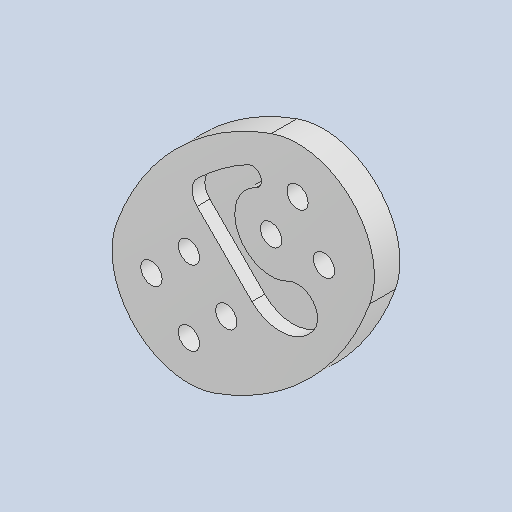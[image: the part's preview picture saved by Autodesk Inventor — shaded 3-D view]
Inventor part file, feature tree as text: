
AUTODESK INVENTOR PART (.ipt)
format: ipt  version: 2023.1 (Build 271208000, 208)  size: 332,800 bytes
history: native  units: mm
features: extrude x2, sketch x2, other x1, projected_geometry x1
ambient origin geometry x8: Origin, YZ Plane, XZ Plane, XY Plane, X Axis, Y Axis, Z Axis, Center Point
bodies: Solid2 (feature_tree)
feature tree (6):
  extrude  "Extrusion2"  Depth=3.0mm TaperAngle=0.0deg
  extrude  "Extrusion3"  Depth=3.0mm
  other  "sesaku"
  sketch  "Sketch2"  dims[d31=40.0mm d33=30.0mm d34=18.0mm d35=9.0mm d36=2.5mm d37=6.2mm d38=360.0deg d39=2.5mm d40=6.2mm d41=360.0deg d42=11.0mm d43=45.0deg d44=3.0mm d45=0.0mm]
  sketch  "Sketch3"  dims[d46=3.0mm d49=3.0mm d52=3.0mm d53=3.0mm d54=3.0mm d55=3.0mm d56=3.0mm d57=1.5mm d58=0.0mm d59=3.0mm d60=2.0mm]
  projected_geometry  "Projected Loop1"
